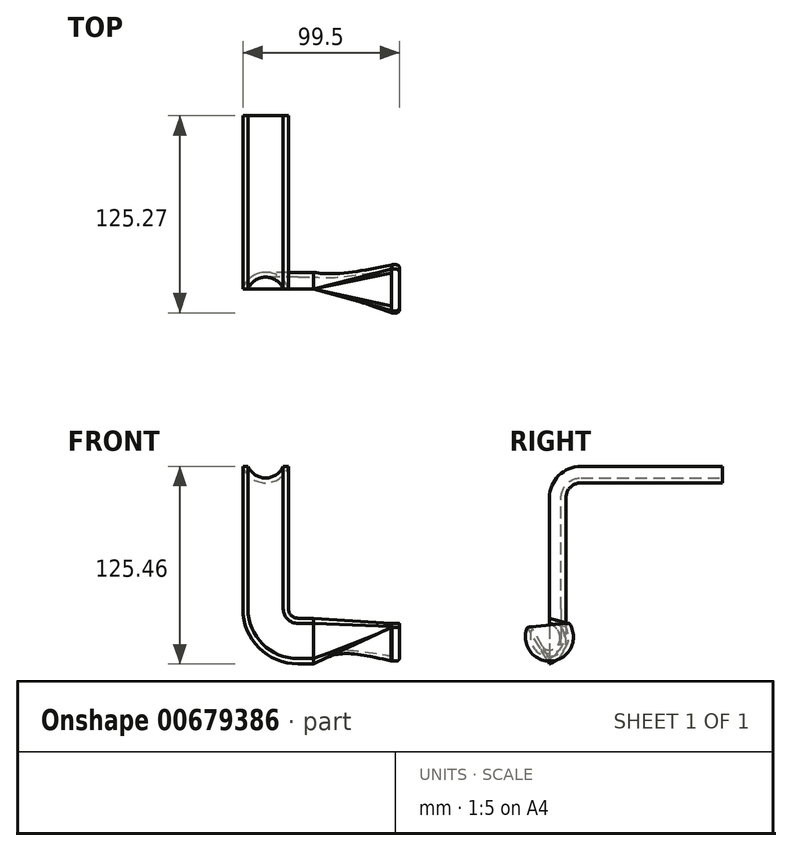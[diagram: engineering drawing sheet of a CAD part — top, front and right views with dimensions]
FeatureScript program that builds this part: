
annotation { "Feature Type Name" : "Feature", "Feature Type Description" : "" }
export const myFeature = defineFeature(function(context is Context, id is Id, definition is map)
    precondition{}
    {
        {
            var Q0;
            Q0=qCreatedBy(makeId("Top.planeOp"),FACE);
            var sketch = newSketch(context, id + "F0", { "sketchPlane" : qUnion([Q0])});
            skLineSegment(sketch, "E0", {"start": v(-15, 0) * mm, "end": v(-11.69, 0) * mm});
            skArc(sketch, "E1", {"start": v(14, 0) * mm, "mid": v(-0.5, 10.48) * mm, "end": v(-15, 0) * mm});
            skArc(sketch, "E2.0", {"start": v(10.69, 0) * mm, "mid": v(-0.5, 7.38) * mm, "end": v(-11.69, 0) * mm});
            skLineSegment(sketch, "E3.trimOffspring", {"start": v(10.69, 0) * mm, "end": v(14, 0) * mm});
            skSolve(sketch);
        }
        {
            var Q0;
            Q0=qCreatedBy(makeId("Right.planeOp"),FACE);
            var sketch = newSketch(context, id + "F1", { "sketchPlane" : qUnion([Q0])});
            skLineSegment(sketch, "E4", {"start": v(0, 0) * mm, "end": v(0, 45) * mm});
            skLineSegment(sketch, "E5", {"start": v(20, 65) * mm, "end": v(110, 65) * mm});
            skPoint(sketch, "E6.visualSharp", {"position": v(0, 65) * mm});
            skArc(sketch, "E6.filletArc", {"start": v(20, 65) * mm, "mid": v(5.86, 59.14) * mm, "end": v(0, 45) * mm});
            skSolve(sketch);
        }
        {
            var Q0;
            Q0=makeQuery(id+"F0.imprint","IMPRINT",FACE,{"disambiguationData":[TD([[makeQuery(id+"F0.imprint","IMPRINT",EDGE,{"derivedFrom":sQuery(id+"F0.wireOp",EDGE,"E0")}),1.0]])]});
            var Q1;
            Q1=sQuery(id+"F1.wireOp",EDGE,"E4");
            var Q2;
            Q2=sQuery(id+"F1.wireOp",EDGE,"E6.filletArc");
            var Q3;
            Q3=sQuery(id+"F1.wireOp",EDGE,"E5");
            sweep(context, id + "F2", {"profiles" : qUnion([Q0]), "path" : qUnion([Q1, Q2, Q3])});
        }
        {
            var Q0;
            Q0=qCreatedBy(makeId("Right.planeOp"),FACE);
            cPlane(context, id + "F3", {"entities" : qUnion([Q0]), "cplaneType" : CPlaneType.OFFSET, "offset" : 79.5 * mm, "width" : 150 * mm, "height" : 150 * mm});
        }
        {
            var Q0;
            Q0=qCreatedBy(makeId("Front.planeOp"),FACE);
            var sketch = newSketch(context, id + "F4", { "sketchPlane" : qUnion([Q0])});
            skLineSegment(sketch, "E7", {"start": v(0, 0) * mm, "end": v(0, -25.46) * mm});
            skLineSegment(sketch, "E8", {"start": v(20, -45.46) * mm, "end": v(30, -45.46) * mm});
            skPoint(sketch, "E9.visualSharp", {"position": v(0, -45.46) * mm});
            skArc(sketch, "E9.filletArc", {"start": v(0, -25.46) * mm, "mid": v(5.86, -39.6) * mm, "end": v(20, -45.46) * mm});
            skSolve(sketch);
        }
        {
            var Q0;
            Q0=qCreatedBy(id+"F3.planeOp",FACE);
            var sketch = newSketch(context, id + "F5", { "sketchPlane" : qUnion([Q0])});
            skArc(sketch, "E10", {"start": v(-13.95, -37.22) * mm, "mid": v(1.48, -58.63) * mm, "end": v(12.5, -34.65) * mm});
            skArc(sketch, "E11.0", {"start": v(-10.88, -37.97) * mm, "mid": v(0.71, -55.58) * mm, "end": v(10.16, -36.73) * mm});
            skLineSegment(sketch, "E12", {"start": v(12.5, -34.65) * mm, "end": v(10.16, -36.73) * mm});
            skLineSegment(sketch, "E13", {"start": v(-10.88, -37.97) * mm, "end": v(-13.95, -37.22) * mm});
            skSolve(sketch);
        }
        {
            var Q0;
            Q0=makeQuery(id+"F0.imprint","IMPRINT",FACE,{"disambiguationData":[TD([[makeQuery(id+"F0.imprint","IMPRINT",EDGE,{"derivedFrom":sQuery(id+"F0.wireOp",EDGE,"E0")}),1.0]])]});
            var Q1;
            Q1=sQuery(id+"F0.wireOp",EDGE,"E1");
            var Q2;
            Q2=sQuery(id+"F0.wireOp",EDGE,"E2.0");
            var Q3;
            Q3=sQuery(id+"F0.wireOp",EDGE,"E3.trimOffspring");
            var Q4;
            Q4=sQuery(id+"F0.wireOp",EDGE,"E0");
            var Q5;
            Q5=sQuery(id+"F5.wireOp",EDGE,"E11.0");
            var Q6;
            Q6=sQuery(id+"F5.wireOp",EDGE,"E10");
            var Q7;
            Q7=sQuery(id+"F5.wireOp",EDGE,"217c170b-dcb2-4ca3-89a6-90ee790057e7");
            var Q8;
            Q8=sQuery(id+"F5.wireOp",EDGE,"692ef912-3e5a-426b-8154-93670f1d0bcc.trimOffspring");
            var Q9;
            Q9=sQuery(id+"F4.wireOp",EDGE,"E9.filletArc");
            var Q10;
            Q10=sQuery(id+"F4.wireOp",EDGE,"E7");
            var Q11;
            Q11=sQuery(id+"F4.wireOp",EDGE,"E8");
            sweep(context, id + "F6", {"operationType" : NewBodyOperationType.ADD, "profiles" : qUnion([Q0]), "surfaceProfiles" : qUnion([Q1, Q2, Q3, Q4, Q5, Q6, Q7, Q8]), "path" : qUnion([Q9, Q10, Q11])});
        }
        {
            var Q1;
            Q1=makeQuery(id+"F6.opSweep","CAP_FACE",FACE,{"disambiguationData":[OSD([sQuery(id+"F0.wireOp",EDGE,"E0"),sQuery(id+"F0.wireOp",EDGE,"E1"),sQuery(id+"F0.wireOp",EDGE,"E2.0"),sQuery(id+"F0.wireOp",EDGE,"E3.trimOffspring"),sQuery(id+"F4.wireOp",VERTEX,"E8.end")])],"isStart":false});
            var Q2;
            Q2=makeQuery(id+"F5.imprint","IMPRINT",FACE,{"disambiguationData":[TD([[makeQuery(id+"F5.imprint","IMPRINT",EDGE,{"derivedFrom":sQuery(id+"F5.wireOp",EDGE,"E10")}),1.0]])]});
            loft(context, id + "F7", {"operationType" : NewBodyOperationType.ADD, "sheetProfilesArray" : [{ "sheetProfileEntities" : qUnion([Q1]) }, { "sheetProfileEntities" : qUnion([Q2]) }]});
        }
        {
            var Q0;
            Q0=makeQuery(id+"F5.imprint","IMPRINT",FACE,{"disambiguationData":[TD([[makeQuery(id+"F5.imprint","IMPRINT",EDGE,{"derivedFrom":sQuery(id+"F5.wireOp",EDGE,"E10")}),1.0]])]});
            var sketch = newSketch(context, id + "F8", { "sketchPlane" : qUnion([Q0])});
            skArc(sketch, "E14.0.0", {"start": v(10.16, -36.73) * mm, "mid": v(0.71, -55.58) * mm, "end": v(-10.88, -37.97) * mm});
            skLineSegment(sketch, "E14.0.1", {"start": v(-10.88, -37.97) * mm, "end": v(-13.95, -37.22) * mm});
            skArc(sketch, "E14.0.2", {"start": v(-13.95, -37.22) * mm, "mid": v(1.48, -58.63) * mm, "end": v(12.5, -34.65) * mm});
            skLineSegment(sketch, "E14.0.3", {"start": v(12.5, -34.65) * mm, "end": v(10.16, -36.73) * mm});
            skLineSegment(sketch, "E15", {"start": v(12.5, -34.65) * mm, "end": v(-13.95, -37.22) * mm});
            skSolve(sketch);
        }
        {
            var Q0;
            Q0=makeQuery(id+"F5.imprint","IMPRINT",FACE,{"disambiguationData":[TD([[makeQuery(id+"F5.imprint","IMPRINT",EDGE,{"derivedFrom":sQuery(id+"F5.wireOp",EDGE,"E10")}),1.0]])]});
            var Q1;
            Q1=makeQuery(id+"F8.imprint","IMPRINT",FACE,{"disambiguationData":[TD([[makeQuery(id+"F8.imprint","IMPRINT",EDGE,{"derivedFrom":sQuery(id+"F8.wireOp",EDGE,"E14.0.0")}),1.0]])]});
            extrude(context, id + "F9", {"entities" : qUnion([Q0, Q1]), "operationType" : NewBodyOperationType.ADD, "depth" : 5 * mm, "offsetDistance" : 25 * mm});
        }
        {
            var Q0;
            Q0=makeQuery(id+"F9.opExtrude","CAP_EDGE",EDGE,{"disambiguationData":[OSD([sQuery(id+"F5.wireOp",EDGE,"E10")])],"isStart":false});
            var Q1;
            {var subQ0=sQuery(id+"F5.wireOp",EDGE,"E10");Q1=makeQuery(id+"F9.boolean.opBoolean","MERGE",EDGE,{"derivedFrom":[makeQuery(id+"F7.opLoft","MID_CAP_EDGE",EDGE,{"disambiguationData":[OSD([subQ0,sQuery(id+"F5.wireOp",EDGE,"E12"),sQuery(id+"F5.wireOp",EDGE,"E13")])],"capPos":1.0}),makeQuery(id+"F9.opExtrude","CAP_EDGE",EDGE,{"disambiguationData":[OSD([subQ0])],"isStart":true})]});}
            fillet(context, id + "F10", {"entities" : qUnion([Q0, Q1]), "radius" : 2 * mm, "tangentPropagation" : true, "allowEdgeOverflow" : false});
        }
    });
